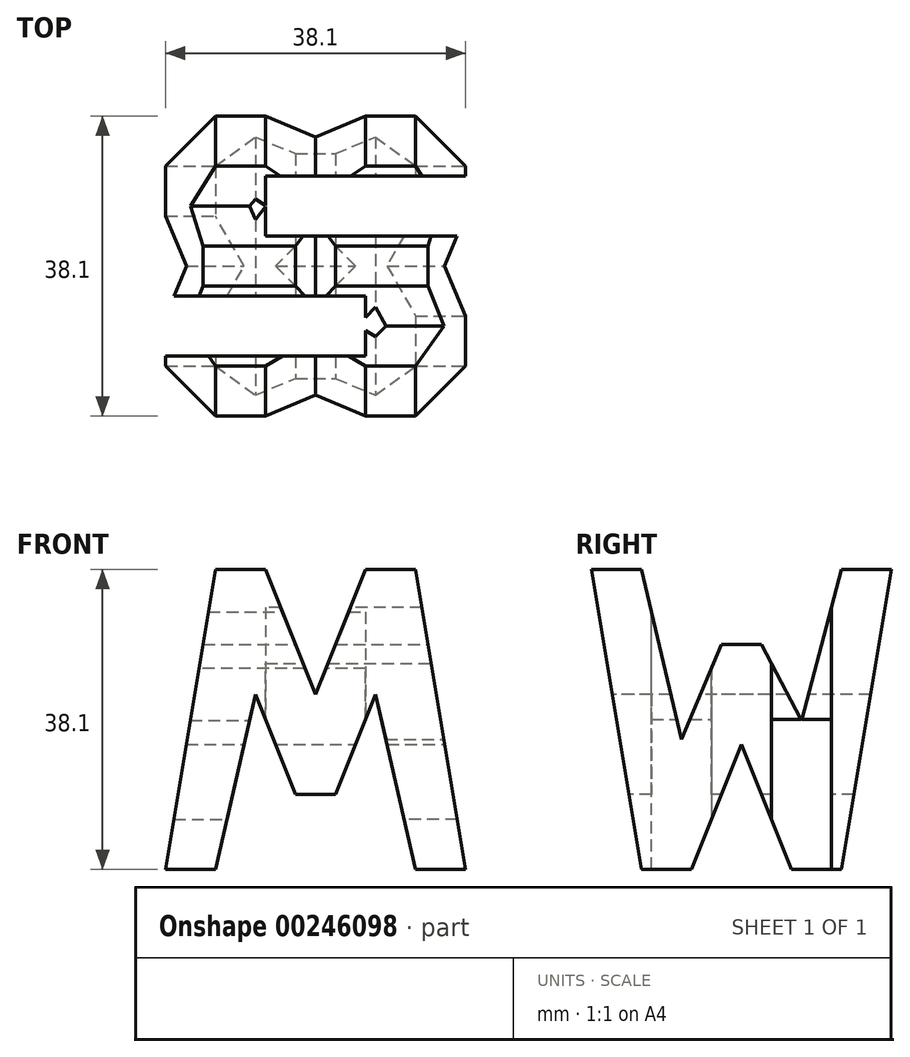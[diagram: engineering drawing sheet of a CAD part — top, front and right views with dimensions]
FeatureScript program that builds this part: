
annotation { "Feature Type Name" : "Feature", "Feature Type Description" : "" }
export const myFeature = defineFeature(function(context is Context, id is Id, definition is map)
    precondition{}
    {
        {
            var Q0;
            Q0=qCreatedBy(makeId("Front.planeOp"),FACE);
            var sketch = newSketch(context, id + "F0", { "sketchPlane" : qUnion([Q0])});
            skPoint(sketch, "E0.start.orphan", {"position": v(0, 38.1) * mm});
            skLineSegment(sketch, "E1.bottom", {"start": v(0, 0) * mm, "end": v(38.1, 0) * mm});
            skLineSegment(sketch, "E1.top", {"start": v(0, 38.1) * mm, "end": v(38.1, 38.1) * mm});
            skLineSegment(sketch, "E1.left", {"start": v(0, 0) * mm, "end": v(0, 38.1) * mm});
            skLineSegment(sketch, "E1.right", {"start": v(38.1, 0) * mm, "end": v(38.1, 38.1) * mm});
            skSolve(sketch);
        }
        {
            var Q0;
            Q0=makeQuery(id+"F0.imprint","IMPRINT",FACE,{"disambiguationData":[TD([[makeQuery(id+"F0.imprint","IMPRINT",EDGE,{"derivedFrom":sQuery(id+"F0.wireOp",EDGE,"E1.bottom")}),1.0]])]});
            extrude(context, id + "F1", {"entities" : qUnion([Q0]), "depth" : 38.1 * mm});
        }
        {
            var Q0;
            Q0=qCreatedBy(makeId("Front.planeOp"),FACE);
            cPlane(context, id + "F2", {"entities" : qUnion([Q0]), "cplaneType" : CPlaneType.OFFSET, "offset" : 38.1 * mm, "width" : 152.4 * mm, "height" : 152.4 * mm});
        }
        {
            var Q0;
            Q0=qCreatedBy(makeId("Right.planeOp"),FACE);
            cPlane(context, id + "F3", {"entities" : qUnion([Q0]), "cplaneType" : CPlaneType.OFFSET, "offset" : 38.1 * mm, "width" : 152.4 * mm, "height" : 152.4 * mm});
        }
        {
            var Q0;
            Q0=qCreatedBy(makeId("Top.planeOp"),FACE);
            cPlane(context, id + "F4", {"entities" : qUnion([Q0]), "cplaneType" : CPlaneType.OFFSET, "offset" : 38.1 * mm, "width" : 152.4 * mm, "height" : 152.4 * mm});
        }
        {
            var Q0;
            Q0=qCreatedBy(id+"F3.planeOp",FACE);
            var sketch = newSketch(context, id + "F5", { "sketchPlane" : qUnion([Q0])});
            skLineSegment(sketch, "E2", {"start": v(0, 0) * mm, "end": v(0, 38.1) * mm});
            skLineSegment(sketch, "E3", {"start": v(0, 38.1) * mm, "end": v(-38.1, 38.1) * mm});
            skLineSegment(sketch, "E4", {"start": v(-38.1, 38.1) * mm, "end": v(-38.1, 0) * mm});
            skLineSegment(sketch, "E5", {"start": v(-38.1, 0) * mm, "end": v(0, 0) * mm});
            skLineSegment(sketch, "E6", {"start": v(-38.1, 38.1) * mm, "end": v(-31.75, 0) * mm});
            skLineSegment(sketch, "E7", {"start": v(-31.75, 38.1) * mm, "end": v(-26.67, 16.5) * mm});
            skLineSegment(sketch, "E8", {"start": v(-26.67, 16.5) * mm, "end": v(-21.59, 28.58) * mm});
            skLineSegment(sketch, "E9", {"start": v(-21.59, 28.58) * mm, "end": v(-16.5, 28.58) * mm});
            skLineSegment(sketch, "E10", {"start": v(-16.5, 28.58) * mm, "end": v(-11.43, 18.9) * mm});
            skLineSegment(sketch, "E11", {"start": v(0, 38.1) * mm, "end": v(-6.35, 0) * mm});
            skLineSegment(sketch, "E12", {"start": v(-12.7, 0) * mm, "end": v(-19.05, 15.88) * mm});
            skLineSegment(sketch, "E13", {"start": v(-19.05, 15.88) * mm, "end": v(-25.4, 0) * mm});
            skPoint(sketch, "E14.end.orphan", {"position": v(-6.35, 37.55) * mm});
            skLineSegment(sketch, "E15", {"start": v(-11.43, 18.9) * mm, "end": v(-6.35, 38.1) * mm});
            skSolve(sketch);
        }
        {
            var Q0;
            {var subQ0=sQuery(id+"F5.wireOp",EDGE,"E7");Q0=makeQuery(id+"F5.imprint","IMPRINT",FACE,{"disambiguationData":[TD([[makeQuery(id+"F5.imprint","IMPRINT",EDGE,{"derivedFrom":subQ0}),1.0]])]});}
            var Q1;
            {var subQ0=sQuery(id+"F5.wireOp",EDGE,"E2");Q1=makeQuery(id+"F5.imprint","IMPRINT",FACE,{"disambiguationData":[TD([[makeQuery(id+"F5.imprint","IMPRINT",EDGE,{"derivedFrom":subQ0}),1.0]])]});}
            var Q2;
            {var subQ0=sQuery(id+"F5.wireOp",EDGE,"E12");Q2=makeQuery(id+"F5.imprint","IMPRINT",FACE,{"disambiguationData":[TD([[makeQuery(id+"F5.imprint","IMPRINT",EDGE,{"derivedFrom":subQ0}),1.0]])]});}
            var Q3;
            {var subQ0=sQuery(id+"F5.wireOp",EDGE,"E4");Q3=makeQuery(id+"F5.imprint","IMPRINT",FACE,{"disambiguationData":[TD([[makeQuery(id+"F5.imprint","IMPRINT",EDGE,{"derivedFrom":subQ0}),1.0]])]});}
            extrude(context, id + "F6", {"entities" : qUnion([Q0, Q1, Q2, Q3]), "operationType" : NewBodyOperationType.REMOVE, "oppositeDirection" : true, "depth" : 38.1 * mm});
        }
        {
            var Q0;
            Q0=qCreatedBy(id+"F2.planeOp",FACE);
            var sketch = newSketch(context, id + "F7", { "sketchPlane" : qUnion([Q0])});
            skLineSegment(sketch, "E16", {"start": v(0, 0) * mm, "end": v(38.1, 0) * mm});
            skLineSegment(sketch, "E17", {"start": v(38.1, 0) * mm, "end": v(38.1, 38.1) * mm});
            skLineSegment(sketch, "E18", {"start": v(38.1, 38.1) * mm, "end": v(0, 38.1) * mm});
            skLineSegment(sketch, "E19", {"start": v(0, 38.1) * mm, "end": v(0, 0) * mm});
            skLineSegment(sketch, "E20", {"start": v(0, 0) * mm, "end": v(6.35, 38.1) * mm});
            skLineSegment(sketch, "E21", {"start": v(6.35, 0) * mm, "end": v(11.43, 22.23) * mm});
            skLineSegment(sketch, "E22", {"start": v(11.43, 22.23) * mm, "end": v(16.51, 9.52) * mm});
            skLineSegment(sketch, "E23", {"start": v(16.51, 9.53) * mm, "end": v(21.59, 9.53) * mm});
            skLineSegment(sketch, "E24", {"start": v(21.59, 9.53) * mm, "end": v(26.67, 22.23) * mm});
            skLineSegment(sketch, "E25", {"start": v(26.67, 22.23) * mm, "end": v(31.75, 0) * mm});
            skLineSegment(sketch, "E26", {"start": v(38.1, 0) * mm, "end": v(31.75, 38.1) * mm});
            skLineSegment(sketch, "E27", {"start": v(25.4, 38.1) * mm, "end": v(19.05, 22.22) * mm});
            skLineSegment(sketch, "E28", {"start": v(19.05, 22.23) * mm, "end": v(12.7, 38.1) * mm});
            skSolve(sketch);
        }
        {
            var Q0;
            {var subQ0=sQuery(id+"F7.wireOp",EDGE,"E19");Q0=makeQuery(id+"F7.imprint","IMPRINT",FACE,{"disambiguationData":[TD([[makeQuery(id+"F7.imprint","IMPRINT",EDGE,{"derivedFrom":subQ0}),1.0]])]});}
            var Q1;
            {var subQ0=sQuery(id+"F7.wireOp",EDGE,"E21");Q1=makeQuery(id+"F7.imprint","IMPRINT",FACE,{"disambiguationData":[TD([[makeQuery(id+"F7.imprint","IMPRINT",EDGE,{"derivedFrom":subQ0}),-1.0]])]});}
            var Q2;
            {var subQ0=sQuery(id+"F7.wireOp",EDGE,"E17");Q2=makeQuery(id+"F7.imprint","IMPRINT",FACE,{"disambiguationData":[TD([[makeQuery(id+"F7.imprint","IMPRINT",EDGE,{"derivedFrom":subQ0}),1.0]])]});}
            var Q3;
            {var subQ0=sQuery(id+"F7.wireOp",EDGE,"E27");Q3=makeQuery(id+"F7.imprint","IMPRINT",FACE,{"disambiguationData":[TD([[makeQuery(id+"F7.imprint","IMPRINT",EDGE,{"derivedFrom":subQ0}),-1.0]])]});}
            extrude(context, id + "F8", {"entities" : qUnion([Q0, Q1, Q2, Q3]), "operationType" : NewBodyOperationType.REMOVE, "oppositeDirection" : true, "depth" : 38.1 * mm});
        }
        {
            var Q0;
            Q0=qCreatedBy(id+"F4.planeOp",FACE);
            var sketch = newSketch(context, id + "F9", { "sketchPlane" : qUnion([Q0])});
            skLineSegment(sketch, "E29", {"start": v(0, 0) * mm, "end": v(38.1, 0) * mm});
            skLineSegment(sketch, "E30", {"start": v(38.1, 0) * mm, "end": v(38.1, -38.1) * mm});
            skLineSegment(sketch, "E31", {"start": v(38.1, -38.1) * mm, "end": v(0, -38.1) * mm});
            skLineSegment(sketch, "E32", {"start": v(0, -38.1) * mm, "end": v(0, 0) * mm});
            skLineSegment(sketch, "E33", {"start": v(38.1, -15.24) * mm, "end": v(12.7, -15.24) * mm});
            skLineSegment(sketch, "E34", {"start": v(12.7, -15.24) * mm, "end": v(12.7, -7.62) * mm});
            skLineSegment(sketch, "E35", {"start": v(12.7, -7.62) * mm, "end": v(38.1, -7.62) * mm});
            skLineSegment(sketch, "E36", {"start": v(38.1, -7.62) * mm, "end": v(38.1, -15.24) * mm});
            skLineSegment(sketch, "E37", {"start": v(0, -22.86) * mm, "end": v(25.4, -22.86) * mm});
            skLineSegment(sketch, "E38", {"start": v(25.4, -22.86) * mm, "end": v(25.4, -30.48) * mm});
            skLineSegment(sketch, "E39", {"start": v(25.4, -30.48) * mm, "end": v(0, -30.48) * mm});
            skLineSegment(sketch, "E40", {"start": v(0, -30.48) * mm, "end": v(0, -22.86) * mm});
            skSolve(sketch);
        }
        {
            var Q0;
            Q0=makeQuery(id+"F9.imprint","IMPRINT",FACE,{"disambiguationData":[TD([[makeQuery(id+"F9.imprint","IMPRINT",EDGE,{"derivedFrom":sQuery(id+"F9.wireOp",EDGE,"E33")}),-1.0]])]});
            var Q1;
            Q1=makeQuery(id+"F9.imprint","IMPRINT",FACE,{"disambiguationData":[TD([[makeQuery(id+"F9.imprint","IMPRINT",EDGE,{"derivedFrom":sQuery(id+"F9.wireOp",EDGE,"E37")}),-1.0]])]});
            extrude(context, id + "F10", {"entities" : qUnion([Q0, Q1]), "operationType" : NewBodyOperationType.REMOVE, "oppositeDirection" : true, "depth" : 38.1 * mm});
        }
    });
